# Revit family: Building-IEC309Connections-GEWISS-67IB-INTERLOCKED-SOCKET-OUTLETS_IP67_WITHOUT_BOTTOM_63A
name_source: partatom
category: Apparecchi elettrici
units: mm (PartAtom-declared; Revit-internal decimal feet)

## family parameters
Condiviso = Sì
Host = Superficie
Mantenere orientamento annotazione = Sì
Punto di calcolo locali = Sì
Quota connettore circolare = Usa diametro
Taglio con vuoti quando caricato = Sì
Tipo di parte = Normale

## types (11) — shared parameters
Catalogue = BUILDING
Catalogue Range = 67 IB
Corpo presa = GEWISS -BLU
Electrocod = 2222
Frequency = 50/60 Hz
Glow Wire Test = 850 °C
Glow wire test: = 850 °C
IDF = 122861de-0204-44ac-8832-c9cd502636ad
IDT = 3210f2e1-5490-4980-ba84-a365430e0752
IP degree = IP67
Immagine tipo = D.jpg
Operating temperature: = -25 +40 °C
Produttore = GEWISS S.p.A.
Prospetto di default = 1219 mm
Protection = NO (SBF)
Rated current (A) = 63
Rated current (In) = 63
Rated frequency (Hz) = 50/60 Hz
SEO = Socket outlet
Shock resistance = IK08
Simbolo presa = PRESAINDSTAGNA : 3P
Struttura = Grigio RAL - 7035
Technical sheet = https://www.gewiss.com
Thermo-pressure with ball = 125
Typology = Vertical
URL = https://www.gewiss.com
Version file RFA = 21.4
With back-mounting box = No
Working temperature = -25 ÷ +40 °C
presa = Giallo
zero-valued in all types: giallo

## per-type parameters (varying)
| type | Colour | Colour: | Descrizione | EAN code | Modello | No. of poles | Number of poles | Rated voltage | Rated voltage: | Reference h |
| GW67360N - 63A 3P+E 220V V.INT.SOCK.O.N.B.9H SBF | Blue | Blue | 63A 3P+E 220V V.INT.SOCK.O.N.B.9H SBF | 8011564742413 | GW67360N | 3P+E | 3P+E | 200 - 250 V | 200 - 250 V | 9 |
| GW67361N - 63A 3P+N+E 220V V.INT.SOCK.O.N.B.9H SBF | Blue | Blue | 63A 3P+N+E 220V V.INT.SOCK.O.N.B.9H SBF | 8011564742420 | GW67361N | 3P+N+E | 3P+N+E | 200 - 250 V | 200 - 250 V | 9 |
| GW67356N - 63A 2P+E 110V V.INT.SOCK.O.N.B.4H SBF | Yellow | Yellow | 63A 2P+E 110V V.INT.SOCK.O.N.B.4H SBF | 8011564742376 | GW67356N | 2P+E | 2P+E | 100 - 130 V | 100 - 130 V | 4 |
| GW67362N - 63A 2P+E 380V V.INT.SOCK.O.N.B.9H SBF | Red | Red | 63A 2P+E 380V V.INT.SOCK.O.N.B.9H SBF | 8011564742437 | GW67362N | 2P+E | 2P+E | 380 - 415 V | 380 - 415 V | 9 |
| GW67363N - 63A 3P+E 380V V.INT.SOCK.O.N.B.6H SBF | Red | Red | 63A 3P+E 380V V.INT.SOCK.O.N.B.6H SBF | 8011564742444 | GW67363N | 3P+E | 3P+E | 380 - 415 V | 380 - 415 V | 6 |
| GW67364N - 63A 3P+N+E 380V V.INT.SOCK.O.N.B.6H SBF | Red | Red | 63A 3P+N+E 380V V.INT.SOCK.O.N.B.6H SBF | 8011564742451 | GW67364N | 3P+N+E | 3P+N+E | 380 - 415 V | 380 - 415 V | 6 |
| GW67357N - 63A 3P+E 110V V.INT.SOCK.O.N.B.4H SBF | Yellow | Yellow | 63A 3P+E 110V V.INT.SOCK.O.N.B.4H SBF | 8011564742383 | GW67357N | 3P+E | 3P+E | 100 - 130 V | 100 - 130 V | 4 |
| GW67358N - 63A 3P+N+E 110V V.INT.SOCK.O.N.B.4H SBF | Yellow | Yellow | 63A 3P+N+E 110V V.INT.SOCK.O.N.B.4H SBF | 8011564742390 | GW67358N | 3P+N+E | 3P+N+E | 100 - 130 V | 100 - 130 V | 4 |
| GW67359N - 63A 2P+E 220V V.INT.SOCK.O.N.B.6H SBF | Blue | Blue | 63A 2P+E 220V V.INT.SOCK.O.N.B.6H SBF | 8011564742406 | GW67359N | 2P+E | 2P+E | 200 - 250 V | 200 - 250 V | 6 |
| GW67366N - 63A 3P+N+E 500V V.INT.SOCK.O.N.B.7H SBF | Black | Black | 63A 3P+N+E 500V V.INT.SOCK.O.N.B.7H SBF | 8011564742475 | GW67366N | 3P+N+E | 3P+N+E | 480 - 500 V | 480 - 500 V | 7 |
| GW67365N - 63A 3P+E 500V V.INT.SOCK.O.N.B.7H SBF | Black | Black | 63A 3P+E 500V V.INT.SOCK.O.N.B.7H SBF | 8011564742468 | GW67365N | 3P+E | 3P+E | 480 - 500 V | 480 - 500 V | 7 |

note: source unit labels omitted for Thermo-pressure with ball — the stored unit's dimension contradicts the parameter name (converter mislabeling)

## geometry (parser evidence)
native form markers: Sweep x7
no freeform markers — native parametric forms only
